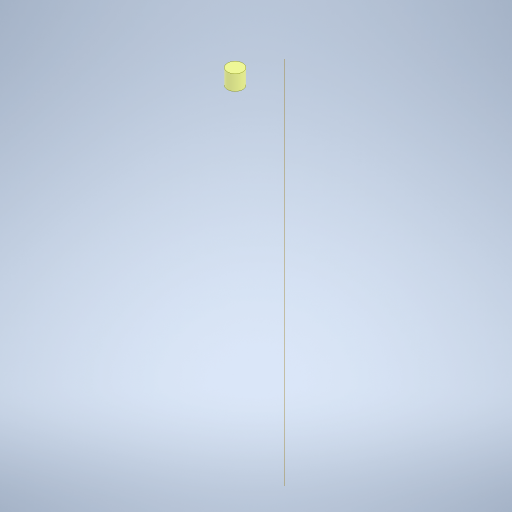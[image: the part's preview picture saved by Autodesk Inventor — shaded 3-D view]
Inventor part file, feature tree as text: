
AUTODESK INVENTOR PART (.ipt)
format: ipt  version: 2024.2 (Build 282272000, 272)  size: 8,395,776 bytes
history: native  units: mm
features: extrude x29, projected_geometry x22, sketch x18, other x14, plane x8, boolean_combine x8, helix x2, pattern_circular x2, fillet x1, split x1, mirror x1, imported_body x1
ambient origin geometry x8: Origin, YZ Plane, XZ Plane, XY Plane, X Axis, Y Axis, Z Axis, Center Point
bodies: Solid27 (feature_tree), Solid35 (feature_tree), Solid36 (feature_tree)
feature tree (107):
  other  "Soft Robot - Cuerpo"
  extrude  "Extrusion47"  TaperAngle=120.0deg  [1 undecoded]
  fillet  "Fillet7"  Radius=25.0mm
  other  "Work Axis3"
  plane  "Work Plane11"
  plane  "Work Plane12"
  sketch  "Sketch32"  dims[d205=3.0mm]
  helix  "Coil4"  [1 undecoded]
  helix  "Coil5"  [1 undecoded]
  plane  "Work Plane13"
  pattern_circular  "Circular Pattern5"  Count=10  [1 undecoded]
  extrude  "Extrusion51"  Depth=10.0mm TaperAngle=0.0deg
  extrude  "Extrusion55"  [1 undecoded]
  boolean_combine  "Combine16"
  extrude  "Extrusion56"  Depth=10.0mm TaperAngle=0.0deg
  boolean_combine  "Combine17"
  plane  "Work Plane17"
  plane  "Work Plane18"
  plane  "Work Plane19"
  split  "Split3"
  extrude  "Extrusion57"  Depth=5.0mm TaperAngle=0.0deg
  boolean_combine  "Combine18"
  extrude  "Extrusion58"  TaperAngle=0.0deg  [1 undecoded]
  boolean_combine  "Combine19"
  sketch  "Sketch44"  dims[d277=5.5mm]
  extrude  "Extrusion59"  Depth=1.0mm
  extrude  "Extrusion60"  Depth=0.1mm
  extrude  "Extrusion61"  Depth=0.5mm TaperAngle=0.0deg
  sketch  "Sketch45"  dims[d278=2.5mm]
  extrude  "Extrusion62"  Depth=0.5mm TaperAngle=0.0deg
  extrude  "Extrusion63"  Depth=10.0mm TaperAngle=0.0deg
  sketch  "Sketch46"  dims[d285=3.0mm d286=100.0mm d287=0.0mm]
  extrude  "Extrusion64"  Depth=0.5mm TaperAngle=0.0deg
  extrude  "Extrusion65"  Depth=0.5mm TaperAngle=0.0deg
  sketch  "Sketch47"  dims[d288=30.0mm d289=360.0deg d291=10.0mm d292=0.0mm]
  extrude  "Extrusion66"  Depth=0.5mm
  plane  "Work Plane20"
  extrude  "Extrusion68"  Depth=0.5mm
  mirror  "Mirror6"
  extrude  "Extrusion69"  Depth=0.5mm TaperAngle=0.0deg
  extrude  "Extrusion70"  Depth=10.0mm
  sketch  "Sketch50"  dims[d295=200.0mm d296=10.0mm d297=0.0mm]
  extrude  "Extrusion71"  TaperAngle=0.0deg  [1 undecoded]
  extrude  "Extrusion72"  Depth=10.0mm TaperAngle=0.0deg
  extrude  "Extrusion73"  Depth=0.5mm
  plane  "Work Plane21"
  extrude  "Extrusion74"  Depth=0.5mm
  pattern_circular  "Circular Pattern6"  [2 undecoded]
  sketch  "Sketch52"  dims[d304=10.0mm d305=0.0mm d306=0.0mm d307=0.0mm]
  extrude  "Extrusion75"  Depth=10.0mm TaperAngle=0.0deg
  extrude  "Extrusion76"  Depth=0.5mm TaperAngle=0.0deg
  extrude  "Extrusion77"  Depth=10.0mm TaperAngle=0.0deg
  extrude  "Extrusion78"  Depth=2.6mm
  extrude  "Extrusion79"  Depth=0.5mm
  boolean_combine  "Combine22"
  boolean_combine  "Combine23"
  boolean_combine  "Combine24"
  boolean_combine  "Combine25"
  extrude  "Extrusion80"  Depth=10.0mm TaperAngle=0.0deg
  extrude  "Extrusion81"  Depth=0.5mm TaperAngle=360.0deg
  extrude  "Extrusion82"  Depth=150.0mm TaperAngle=0.0deg
  sketch  "Sketch5"  dims[d47=120.0deg d48=120.0deg d49=25.0mm d50=3.0mm d203=100.0mm d204=0.0mm]
  sketch  "Sketch36"  dims[d235=0.0mm]
  projected_geometry  "Projected Loop43"
  projected_geometry  "Projected Loop46"
  sketch  "Sketch40"  dims[d238=12.0mm d239=89.0mm d240=80.0mm d241=0.0mm d242=90.0deg d243=90.0deg d244=90.0deg d245=90.0deg d246=12.0mm d247=89.0mm d248=80.0mm d249=0.0mm d250=90.0deg d251=90.0deg d252=90.0deg d253=90.0deg d254=90.0deg]
  projected_geometry  "Projected Loop47"
  other  "Insertos PVA"
  sketch  "Sketch41"  dims[d258=3.0mm]
  projected_geometry  "Projected Loop48"
  sketch  "Sketch42"  dims[d271=1.5mm]
  sketch  "Sketch43"  dims[d273=218.25mm d274=0.0mm]
  projected_geometry  "Projected Loop49"
  other  "Soft Robot - Tapas"
  projected_geometry  "Projected Loop50"
  projected_geometry  "Projected Loop51"
  projected_geometry  "Projected Loop52"
  projected_geometry  "Projected Loop53"
  other  "Tapa Inferior"
  projected_geometry  "Projected Loop54"
  projected_geometry  "Projected Loop55"
  projected_geometry  "Projected Loop56"
  projected_geometry  "Projected Loop57"
  projected_geometry  "Projected Loop58"
  projected_geometry  "Projected Loop59"
  projected_geometry  "Projected Loop60"
  sketch  "Sketch49"  dims[d293=-5.5mm d294=-5.5mm]
  other  "Molde - Vaso"
  projected_geometry  "Projected Loop62"
  projected_geometry  "Projected Loop63"
  projected_geometry  "Projected Loop64"
  projected_geometry  "Projected Loop65"
  imported_body  "Base"
  sketch  "Sketch51"  dims[d298=10.0mm d299=0.0mm d301=5.0mm d302=0.0mm]
  other  "Inserto 1"
  other  "Inserto 2"
  other  "Inserto 3"
  sketch  "Sketch53"  dims[d308=12.0mm d309=1.0mm]
  projected_geometry  "Projected Loop66"
  other  "Cuerpo - Simplificado"
  sketch  "Sketch54"  dims[d310=0.1mm d311=0.1mm]
  projected_geometry  "Projected Loop67"
  other  "fijador"
  sketch  "Sketch55"  dims[d312=0.1mm d313=15.0mm d314=0.0mm d315=14.5mm d316=0.0mm d317=10.0mm d318=0.0mm d319=9.5mm d320=0.0mm d322=1.0mm d323=0.0mm d326=0.4mm d327=1.0mm d328=1.0mm d329=0.0mm d330=10.0mm d331=0.0mm d332=0.0mm d333=10.0mm d334=0.0mm d335=1.0mm d336=1.0mm d337=1.0mm d338=10.0mm d339=0.0mm d340=15.0mm d341=0.0mm d342=10.0mm d343=0.0mm d344=2.6mm d345=9.8mm d346=10.0mm d347=0.0mm d348=30.0mm d349=360.0deg d351=150.0mm d352=0.0mm d353=150.0mm d354=0.0mm d355=150.0mm d356=0.0mm d357=150.0mm d358=0.0mm d359=150.0mm d360=0.0mm d361=150.0mm d362=0.0mm d363=5.0mm d364=5.0mm d365=0.0mm d366=5.0mm d367=5.0mm d368=0.0mm d22=0.0mm d23=0.0mm d24=0.0mm d25=0.0mm d132=0.5mm d133=0.872665mm d134=0.5mm d135=0.872665mm d300=0.5mm]
  other  "ROI"
  other  "Tapa Superior"
  other  "Adaptadores"
note: 9 required parameter values undecoded (feature->parameter linkage not recoverable at this tier; creation-order binding heuristic only, values carry confidence <= 0.55)
